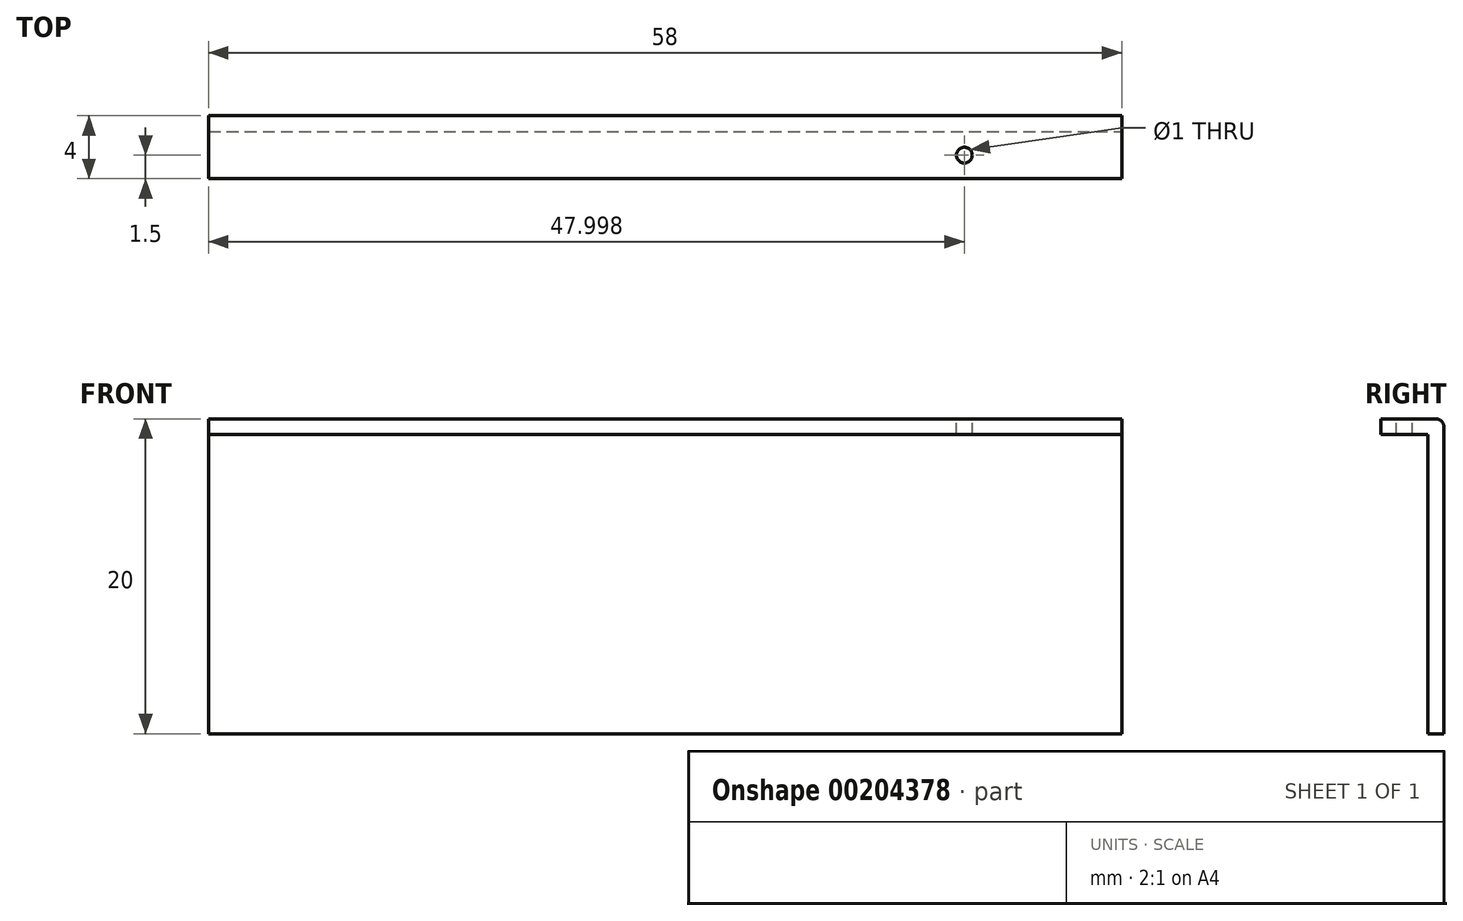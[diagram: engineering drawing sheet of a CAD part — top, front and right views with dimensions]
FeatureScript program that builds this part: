
annotation { "Feature Type Name" : "Feature", "Feature Type Description" : "" }
export const myFeature = defineFeature(function(context is Context, id is Id, definition is map)
    precondition{}
    {
        {
            var Q0;
            Q0=qCreatedBy(makeId("Front.planeOp"),FACE);
            var sketch = newSketch(context, id + "F0", { "sketchPlane" : qUnion([Q0])});
            skLineSegment(sketch, "E0.bottom", {"start": v(-19.41, 19.66) * mm, "end": v(38.59, 19.66) * mm});
            skLineSegment(sketch, "E0.top", {"start": v(-19.41, -0.34) * mm, "end": v(38.59, -0.34) * mm});
            skLineSegment(sketch, "E0.left", {"start": v(-19.41, 19.66) * mm, "end": v(-19.41, -0.34) * mm});
            skLineSegment(sketch, "E0.right", {"start": v(38.59, 19.66) * mm, "end": v(38.59, -0.34) * mm});
            skSolve(sketch);
        }
        {
            var Q0;
            Q0 = qSketchRegion(id + "F0", true);
            extrude(context, id + "F1", {"entities" : qUnion([Q0]), "depth" : 4 * mm});
        }
        {
            var Q0;
            Q0=makeQuery(id+"F1.opExtrude","CAP_FACE",FACE,{"disambiguationData":[OSD([sQuery(id+"F0.wireOp",EDGE,"E0.bottom"),sQuery(id+"F0.wireOp",EDGE,"E0.top"),sQuery(id+"F0.wireOp",EDGE,"E0.left"),sQuery(id+"F0.wireOp",EDGE,"E0.right")])],"isStart":false});
            shell(context, id + "F2", {"entities" : qUnion([Q0]), "thickness" : 1 * mm});
        }
        {
            var Q0;
            Q0=makeQuery(id+"F1.opExtrude","CAP_FACE",FACE,{"disambiguationData":[OSD([sQuery(id+"F0.wireOp",EDGE,"E0.bottom"),sQuery(id+"F0.wireOp",EDGE,"E0.top"),sQuery(id+"F0.wireOp",EDGE,"E0.left"),sQuery(id+"F0.wireOp",EDGE,"E0.right")])],"isStart":false});
            var sketch = newSketch(context, id + "F3", { "sketchPlane" : qUnion([Q0])});
            skLineSegment(sketch, "E1.bottom", {"start": v(37.59, 18.66) * mm, "end": v(38.59, 18.66) * mm});
            skLineSegment(sketch, "E1.top", {"start": v(37.59, 0.66) * mm, "end": v(38.59, 0.66) * mm});
            skLineSegment(sketch, "E1.left", {"start": v(37.59, 18.66) * mm, "end": v(37.59, 0.66) * mm});
            skLineSegment(sketch, "E1.right", {"start": v(38.59, 18.66) * mm, "end": v(38.59, 0.66) * mm});
            skLineSegment(sketch, "E2.bottom", {"start": v(38.59, -0.34) * mm, "end": v(-19.41, -0.34) * mm});
            skLineSegment(sketch, "E2.top", {"start": v(38.59, 0.66) * mm, "end": v(-19.41, 0.66) * mm});
            skLineSegment(sketch, "E2.left", {"start": v(38.59, -0.34) * mm, "end": v(38.59, 0.66) * mm});
            skLineSegment(sketch, "E2.right", {"start": v(-19.41, -0.34) * mm, "end": v(-19.41, 0.66) * mm});
            skLineSegment(sketch, "E3.bottom", {"start": v(-18.41, 18.66) * mm, "end": v(-19.41, 18.66) * mm});
            skLineSegment(sketch, "E3.top", {"start": v(-18.41, 0.66) * mm, "end": v(-19.41, 0.66) * mm});
            skLineSegment(sketch, "E3.left", {"start": v(-18.41, 18.66) * mm, "end": v(-18.41, 0.66) * mm});
            skLineSegment(sketch, "E3.right", {"start": v(-19.41, 18.66) * mm, "end": v(-19.41, 0.66) * mm});
            skSolve(sketch);
        }
        {
            var Q0;
            Q0=makeQuery(id+"F3.imprint","IMPRINT",FACE,{"disambiguationData":[TD([[makeQuery(id+"F3.imprint","IMPRINT",EDGE,{"derivedFrom":sQuery(id+"F3.wireOp",EDGE,"E3.bottom")}),1.0]])]});
            var Q1;
            Q1=makeQuery(id+"F3.imprint","IMPRINT",FACE,{"disambiguationData":[TD([[makeQuery(id+"F3.imprint","IMPRINT",EDGE,{"derivedFrom":sQuery(id+"F3.wireOp",EDGE,"E2.bottom")}),1.0]])]});
            var Q2;
            Q2=makeQuery(id+"F3.imprint","IMPRINT",FACE,{"disambiguationData":[TD([[makeQuery(id+"F3.imprint","IMPRINT",EDGE,{"derivedFrom":sQuery(id+"F3.wireOp",EDGE,"E1.bottom")}),-1.0]])]});
            extrude(context, id + "F4", {"entities" : qUnion([Q0, Q1, Q2]), "operationType" : NewBodyOperationType.REMOVE, "oppositeDirection" : true, "depth" : 3 * mm});
        }
        {
            var Q0;
            Q0=makeQuery(id+"F1.opExtrude","CAP_EDGE",EDGE,{"disambiguationData":[OSD([sQuery(id+"F0.wireOp",EDGE,"E0.bottom")])],"isStart":true});
            fillet(context, id + "F5", {"entities" : qUnion([Q0]), "radius" : 0.5 * mm, "tangentPropagation" : true, "allowEdgeOverflow" : false});
        }
        {
            var Q0;
            Q0=makeQuery(id+"F1.opExtrude","SWEPT_FACE",FACE,{"disambiguationData":[OSD([sQuery(id+"F0.wireOp",EDGE,"E0.bottom")])]});
            var sketch = newSketch(context, id + "F6", { "sketchPlane" : qUnion([Q0])});
            skPoint(sketch, "E4", {"position": v(28.59, -2.5) * mm});
            skSolve(sketch);
        }
        {
            var Q0;
            Q0=sQuery(id+"F6.wireOp",VERTEX,"E4");
            var Q1;
            Q1=makeQuery(id+"F1.opExtrude","SWEPT_BODY",BODY,{"disambiguationData":[OSD([sQuery(id+"F0.wireOp",EDGE,"E0.bottom"),sQuery(id+"F0.wireOp",EDGE,"E0.top"),sQuery(id+"F0.wireOp",EDGE,"E0.left"),sQuery(id+"F0.wireOp",EDGE,"E0.right")])]});
            hole(context, id + "F7", {"style" : HoleStyle.SIMPLE, "endStyle" : HoleEndStyle.BLIND, "holeDiameter" : 1 * mm, "holeDepth" : 1 * mm, "locations" : qUnion([Q0]), "scope" : qUnion([Q1])});
        }
    });
